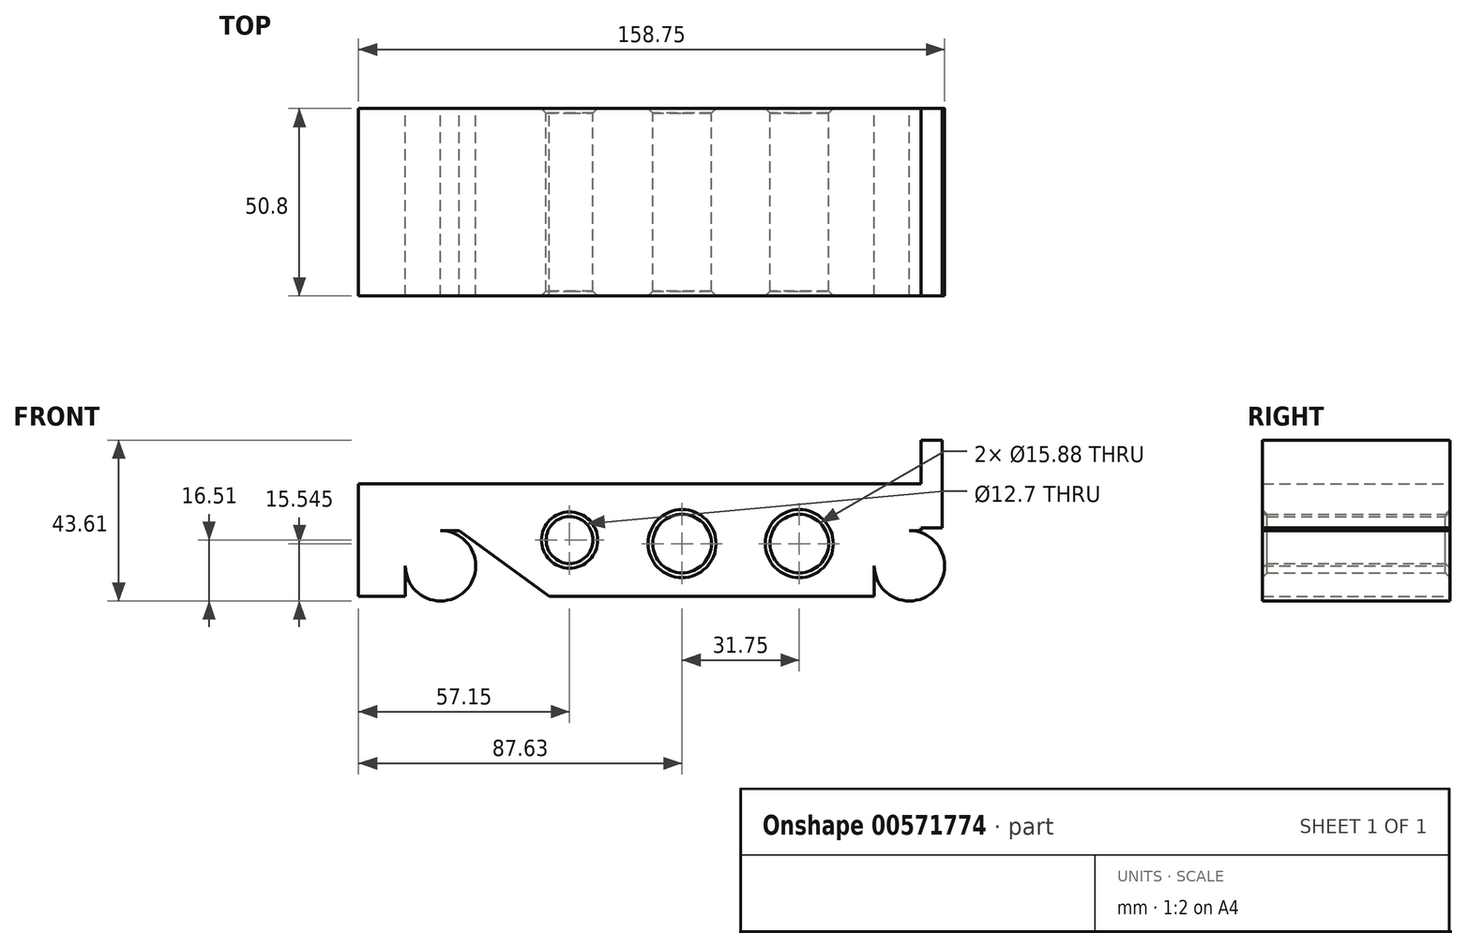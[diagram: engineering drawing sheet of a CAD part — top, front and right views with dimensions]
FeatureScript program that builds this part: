
annotation { "Feature Type Name" : "Feature", "Feature Type Description" : "" }
export const myFeature = defineFeature(function(context is Context, id is Id, definition is map)
    precondition{}
    {
        {
            var Q0;
            Q0=qCreatedBy(makeId("Front.planeOp"),FACE);
            var sketch = newSketch(context, id + "F0", { "sketchPlane" : qUnion([Q0])});
            skLineSegment(sketch, "E0.bottom", {"start": v(0, 30.48) * mm, "end": v(152.4, 30.48) * mm});
            skLineSegment(sketch, "E0.top", {"start": v(0, 0) * mm, "end": v(12.7, 0) * mm});
            skLineSegment(sketch, "E0.left", {"start": v(0, 30.48) * mm, "end": v(0, 0) * mm});
            skLineSegment(sketch, "E0.right", {"start": v(152.4, 30.48) * mm, "end": v(152.4, 17.78) * mm});
            skLineSegment(sketch, "E1", {"start": v(12.7, 0) * mm, "end": v(12.7, 17.78) * mm});
            skLineSegment(sketch, "E2", {"start": v(12.7, 17.78) * mm, "end": v(27.25, 17.78) * mm});
            skLineSegment(sketch, "E3", {"start": v(27.25, 17.78) * mm, "end": v(51.69, 0) * mm});
            skLineSegment(sketch, "E4", {"start": v(139.7, 0) * mm, "end": v(139.7, 17.78) * mm});
            skLineSegment(sketch, "E5", {"start": v(139.7, 17.78) * mm, "end": v(152.4, 17.78) * mm});
            skLineSegment(sketch, "E6.bottom", {"start": v(152.4, 42.34) * mm, "end": v(158.06, 42.34) * mm});
            skLineSegment(sketch, "E6.top", {"start": v(152.4, 18.54) * mm, "end": v(158.06, 18.54) * mm});
            skLineSegment(sketch, "E6.left", {"start": v(152.4, 42.34) * mm, "end": v(152.4, 18.54) * mm});
            skLineSegment(sketch, "E6.right", {"start": v(158.06, 42.34) * mm, "end": v(158.06, 18.54) * mm});
            skCircle(sketch, "E7", {"center": v(22.23, 8.26) * mm, "radius": 9.53 * mm});
            skCircle(sketch, "E8", {"center": v(149.23, 8.26) * mm, "radius": 9.53 * mm});
            skPoint(sketch, "E9.orphan", {"position": v(152.4, 0) * mm});
            skLineSegment(sketch, "E10.trimOffspring", {"start": v(51.69, 0) * mm, "end": v(139.7, 0) * mm});
            skCircle(sketch, "E11", {"center": v(119.38, 14.27) * mm, "radius": 7.94 * mm});
            skCircle(sketch, "E12", {"center": v(87.63, 14.27) * mm, "radius": 7.94 * mm});
            skCircle(sketch, "E13", {"center": v(57.15, 15.24) * mm, "radius": 6.35 * mm});
            skSolve(sketch);
        }
        {
            var Q0;
            Q0 = qSketchRegion(id + "F0", true);
            extrude(context, id + "F1", {"entities" : qUnion([Q0]), "depth" : 25.4 * mm, "offsetDistance" : 25.4 * mm, "hasSecondDirection" : true, "secondDirectionOppositeDirection" : true, "secondDirectionDepth" : 25.4 * mm});
        }
        {
            var Q0;
            Q0=makeQuery(id+"F1.opExtrude","CAP_EDGE",EDGE,{"disambiguationData":[OSD([sQuery(id+"F0.wireOp",EDGE,"E13")])],"isStart":false});
            var Q1;
            Q1=makeQuery(id+"F1.opExtrude","CAP_EDGE",EDGE,{"disambiguationData":[OSD([sQuery(id+"F0.wireOp",EDGE,"E12")])],"isStart":false});
            var Q2;
            Q2=makeQuery(id+"F1.opExtrude","CAP_EDGE",EDGE,{"disambiguationData":[OSD([sQuery(id+"F0.wireOp",EDGE,"E11")])],"isStart":false});
            var Q3;
            Q3=makeQuery(id+"F1.opExtrude","CAP_EDGE",EDGE,{"disambiguationData":[OSD([sQuery(id+"F0.wireOp",EDGE,"E11")])],"isStart":true});
            var Q4;
            Q4=makeQuery(id+"F1.opExtrude","CAP_EDGE",EDGE,{"disambiguationData":[OSD([sQuery(id+"F0.wireOp",EDGE,"E12")])],"isStart":true});
            var Q5;
            Q5=makeQuery(id+"F1.opExtrude","CAP_EDGE",EDGE,{"disambiguationData":[OSD([sQuery(id+"F0.wireOp",EDGE,"E13")])],"isStart":true});
            chamfer(context, id + "F2", {"entities" : qUnion([Q0, Q1, Q2, Q3, Q4, Q5]), "width" : 1.27 * mm, "tangentPropagation" : true});
        }
    });
